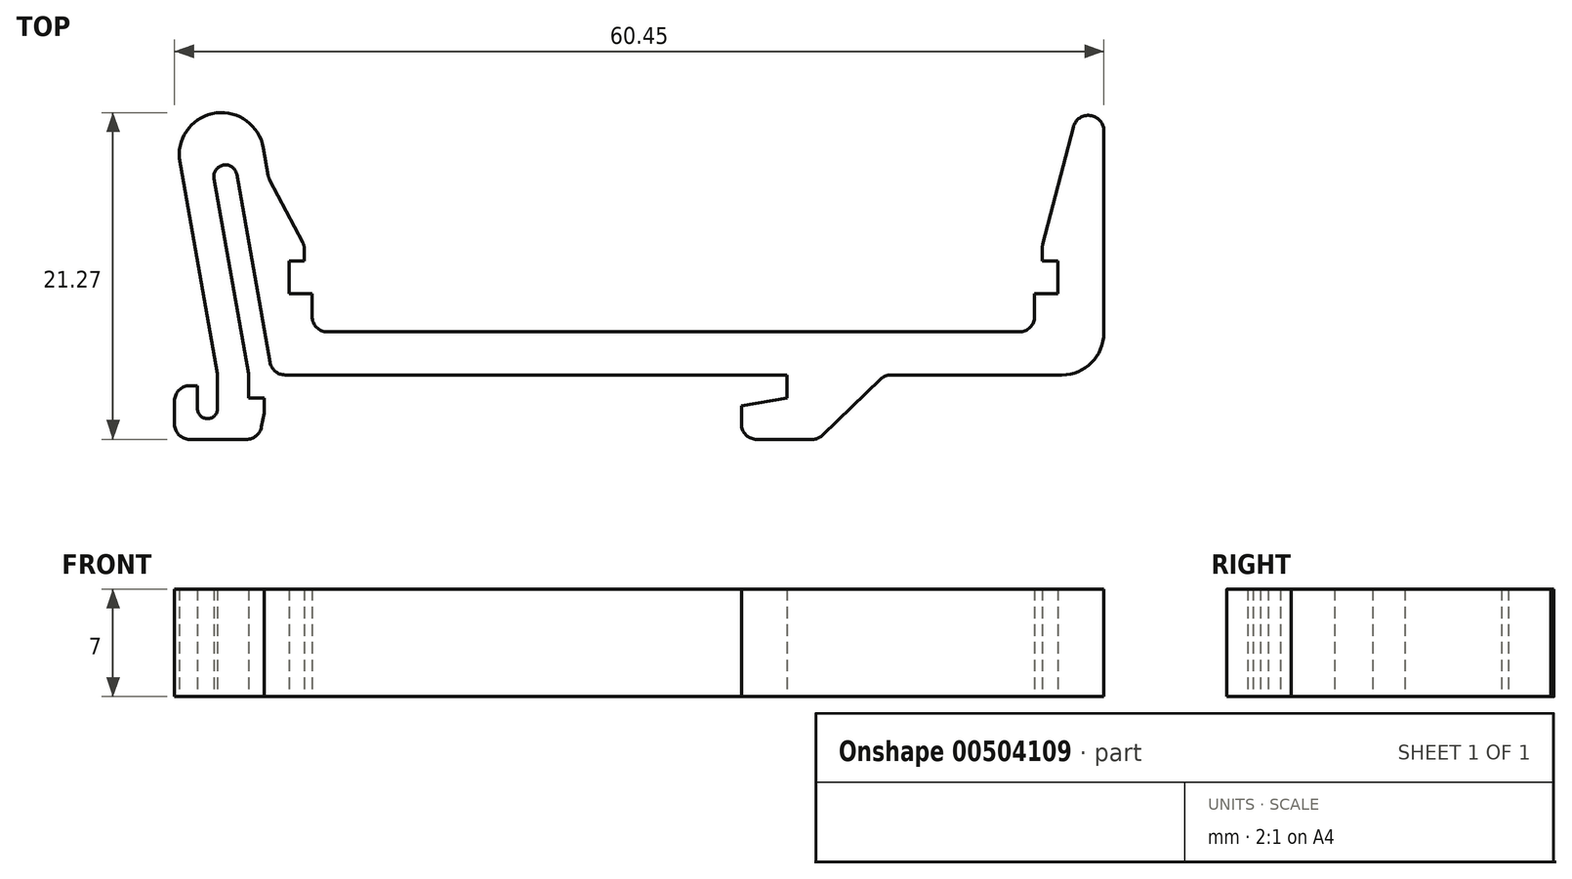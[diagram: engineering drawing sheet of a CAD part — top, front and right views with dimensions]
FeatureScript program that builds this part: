
annotation { "Feature Type Name" : "Feature", "Feature Type Description" : "" }
export const myFeature = defineFeature(function(context is Context, id is Id, definition is map)
    precondition{}
    {
        {
            var Q0;
            Q0=qCreatedBy(makeId("Top.planeOp"),FACE);
            var sketch = newSketch(context, id + "F0", { "sketchPlane" : qUnion([Q0])});
            skLineSegment(sketch, "E0", {"start": v(-27.83, -12.83) * mm, "end": v(-27.83, -9.33) * mm});
            skLineSegment(sketch, "E1", {"start": v(-27.83, -9.33) * mm, "end": v(-26.33, -9.33) * mm});
            skLineSegment(sketch, "E2", {"start": v(-26.33, -9.33) * mm, "end": v(-26.33, -10.83) * mm});
            skLineSegment(sketch, "E3", {"start": v(-25.26, 4.16) * mm, "end": v(-23, -8.63) * mm});
            skLineSegment(sketch, "E4", {"start": v(-23, -8.63) * mm, "end": v(-23, -10.13) * mm});
            skLineSegment(sketch, "E5", {"start": v(-22, -10.13) * mm, "end": v(-23, -10.13) * mm});
            skLineSegment(sketch, "E6", {"start": v(-27.83, -12.83) * mm, "end": v(-22.33, -12.83) * mm});
            skLineSegment(sketch, "E7", {"start": v(-19.38, -0.23) * mm, "end": v(-19.38, -1.23) * mm});
            skLineSegment(sketch, "E8", {"start": v(-19.38, -1.23) * mm, "end": v(-20.38, -1.23) * mm});
            skLineSegment(sketch, "E9", {"start": v(-20.38, -1.23) * mm, "end": v(-20.38, -3.33) * mm});
            skLineSegment(sketch, "E10", {"start": v(-20.38, -3.33) * mm, "end": v(-18.88, -3.33) * mm});
            skLineSegment(sketch, "E11", {"start": v(-18.88, -3.33) * mm, "end": v(-18.88, -5.83) * mm});
            skLineSegment(sketch, "E12", {"start": v(-18.88, -5.83) * mm, "end": v(18.4, -5.83) * mm});
            skLineSegment(sketch, "E13", {"start": v(-23.78, 4.42) * mm, "end": v(-21.48, -8.63) * mm});
            skLineSegment(sketch, "E14", {"start": v(-21.48, -8.63) * mm, "end": v(12, -8.63) * mm});
            skLineSegment(sketch, "E15", {"start": v(12, -8.63) * mm, "end": v(12, -10.13) * mm});
            skLineSegment(sketch, "E16", {"start": v(12, -10.13) * mm, "end": v(9.04, -10.63) * mm});
            skLineSegment(sketch, "E17", {"start": v(9.04, -12.83) * mm, "end": v(14.04, -12.83) * mm});
            skLineSegment(sketch, "E18", {"start": v(28.12, -5.83) * mm, "end": v(28.12, -3.33) * mm});
            skLineSegment(sketch, "E19", {"start": v(29.62, -3.33) * mm, "end": v(29.62, -1.23) * mm});
            skLineSegment(sketch, "E20", {"start": v(28.62, -1.23) * mm, "end": v(29.62, -1.23) * mm});
            skLineSegment(sketch, "E21", {"start": v(28.62, -1.23) * mm, "end": v(28.62, -0.23) * mm});
            skLineSegment(sketch, "E22", {"start": v(30.63, 7.5) * mm, "end": v(28.62, -0.23) * mm});
            skLineSegment(sketch, "E23", {"start": v(32.62, 7.25) * mm, "end": v(32.62, -5.9) * mm});
            skArc(sketch, "E24", {"start": v(-22.06, 6.16) * mm, "mid": v(-25.11, 8.42) * mm, "end": v(-27.52, 5.49) * mm});
            skLineSegment(sketch, "E25", {"start": v(28.12, -3.33) * mm, "end": v(29.62, -3.33) * mm});
            skArc(sketch, "E26", {"start": v(-23.78, 4.42) * mm, "mid": v(-24.65, 5.03) * mm, "end": v(-25.26, 4.16) * mm});
            skLineSegment(sketch, "E27", {"start": v(9.04, -10.63) * mm, "end": v(9.04, -12.83) * mm});
            skArc(sketch, "E28", {"start": v(32.62, 7.25) * mm, "mid": v(31.74, 8.25) * mm, "end": v(30.63, 7.5) * mm});
            skLineSegment(sketch, "E29", {"start": v(-22.06, 6.16) * mm, "end": v(-21.71, 4.2) * mm});
            skLineSegment(sketch, "E30", {"start": v(-21.71, 4.2) * mm, "end": v(-19.38, -0.23) * mm});
            skLineSegment(sketch, "E31", {"start": v(14.04, -12.83) * mm, "end": v(18.4, -8.63) * mm});
            skLineSegment(sketch, "E32", {"start": v(28.12, -5.83) * mm, "end": v(18.4, -5.83) * mm});
            skLineSegment(sketch, "E33", {"start": v(18.4, -5.83) * mm, "end": v(18.4, -8.63) * mm, "construction": true});
            skLineSegment(sketch, "E34", {"start": v(18.4, -8.63) * mm, "end": v(29.89, -8.63) * mm});
            skArc(sketch, "E35", {"start": v(29.89, -8.63) * mm, "mid": v(31.82, -7.84) * mm, "end": v(32.62, -5.9) * mm});
            skLineSegment(sketch, "E36", {"start": v(-25.03, -8.63) * mm, "end": v(-27.52, 5.49) * mm});
            skLineSegment(sketch, "E37", {"start": v(-25.03, -8.63) * mm, "end": v(-25.03, -10.83) * mm});
            skLineSegment(sketch, "E38", {"start": v(-22, -10.13) * mm, "end": v(-22, -11.13) * mm});
            skLineSegment(sketch, "E39", {"start": v(-22, -11.13) * mm, "end": v(-22.33, -12.83) * mm});
            skArc(sketch, "E40", {"start": v(-26.33, -10.83) * mm, "mid": v(-25.68, -11.48) * mm, "end": v(-25.03, -10.83) * mm});
            skSolve(sketch);
        }
        {
            var Q0;
            Q0 = qSketchRegion(id + "F0", true);
            extrude(context, id + "F1", {"entities" : qUnion([Q0]), "depth" : 7 * mm});
        }
        {
            var Q0;
            Q0=makeQuery(id+"F1.opExtrude","SWEPT_EDGE",EDGE,{"disambiguationData":[OSD([sQuery(id+"F0.wireOp",EDGE,"E17"),sQuery(id+"F0.wireOp",EDGE,"E31")])]});
            var Q1;
            Q1=makeQuery(id+"F1.opExtrude","SWEPT_EDGE",EDGE,{"disambiguationData":[OSD([sQuery(id+"F0.wireOp",EDGE,"E0"),sQuery(id+"F0.wireOp",EDGE,"E6")])]});
            var Q2;
            Q2=makeQuery(id+"F1.opExtrude","SWEPT_EDGE",EDGE,{"disambiguationData":[OSD([sQuery(id+"F0.wireOp",EDGE,"E6"),sQuery(id+"F0.wireOp",EDGE,"E39")])]});
            var Q3;
            Q3=makeQuery(id+"F1.opExtrude","SWEPT_EDGE",EDGE,{"disambiguationData":[OSD([sQuery(id+"F0.wireOp",EDGE,"E36"),sQuery(id+"F0.wireOp",EDGE,"E37")])]});
            var Q4;
            Q4=makeQuery(id+"F1.opExtrude","SWEPT_EDGE",EDGE,{"disambiguationData":[OSD([sQuery(id+"F0.wireOp",EDGE,"E31"),sQuery(id+"F0.wireOp",EDGE,"E34")])]});
            var Q5;
            Q5=makeQuery(id+"F1.opExtrude","SWEPT_EDGE",EDGE,{"disambiguationData":[OSD([sQuery(id+"F0.wireOp",EDGE,"E17"),sQuery(id+"F0.wireOp",EDGE,"E27")])]});
            var Q6;
            Q6=makeQuery(id+"F1.opExtrude","SWEPT_EDGE",EDGE,{"disambiguationData":[OSD([sQuery(id+"F0.wireOp",EDGE,"E29"),sQuery(id+"F0.wireOp",EDGE,"E30")])]});
            var Q7;
            Q7=makeQuery(id+"F1.opExtrude","SWEPT_EDGE",EDGE,{"disambiguationData":[OSD([sQuery(id+"F0.wireOp",EDGE,"E21"),sQuery(id+"F0.wireOp",EDGE,"E22")])]});
            var Q8;
            Q8=makeQuery(id+"F1.opExtrude","SWEPT_EDGE",EDGE,{"disambiguationData":[OSD([sQuery(id+"F0.wireOp",EDGE,"E7"),sQuery(id+"F0.wireOp",EDGE,"E30")])]});
            var Q9;
            Q9=makeQuery(id+"F1.opExtrude","SWEPT_EDGE",EDGE,{"disambiguationData":[OSD([sQuery(id+"F0.wireOp",EDGE,"E11"),sQuery(id+"F0.wireOp",EDGE,"E12")])]});
            var Q10;
            Q10=makeQuery(id+"F1.opExtrude","SWEPT_EDGE",EDGE,{"disambiguationData":[OSD([sQuery(id+"F0.wireOp",EDGE,"E13"),sQuery(id+"F0.wireOp",EDGE,"E14")])]});
            var Q11;
            Q11=makeQuery(id+"F1.opExtrude","SWEPT_EDGE",EDGE,{"disambiguationData":[OSD([sQuery(id+"F0.wireOp",EDGE,"E18"),sQuery(id+"F0.wireOp",EDGE,"E32")])]});
            var Q12;
            Q12=makeQuery(id+"F1.opExtrude","SWEPT_EDGE",EDGE,{"disambiguationData":[OSD([sQuery(id+"F0.wireOp",EDGE,"E3"),sQuery(id+"F0.wireOp",EDGE,"E4")])]});
            var Q13;
            Q13=makeQuery(id+"F1.opExtrude","SWEPT_EDGE",EDGE,{"disambiguationData":[OSD([sQuery(id+"F0.wireOp",EDGE,"E36"),sQuery(id+"F0.wireOp",EDGE,"E37")])]});
            var Q14;
            Q14=makeQuery(id+"F1.opExtrude","SWEPT_EDGE",EDGE,{"disambiguationData":[OSD([sQuery(id+"F0.wireOp",EDGE,"E0"),sQuery(id+"F0.wireOp",EDGE,"E1")])]});
            fillet(context, id + "F2", {"entities" : qUnion([Q0, Q1, Q2, Q3, Q4, Q5, Q6, Q7, Q8, Q9, Q10, Q11, Q12, Q13, Q14]), "radius" : 1 * mm, "tangentPropagation" : true, "allowEdgeOverflow" : false});
        }
    });
